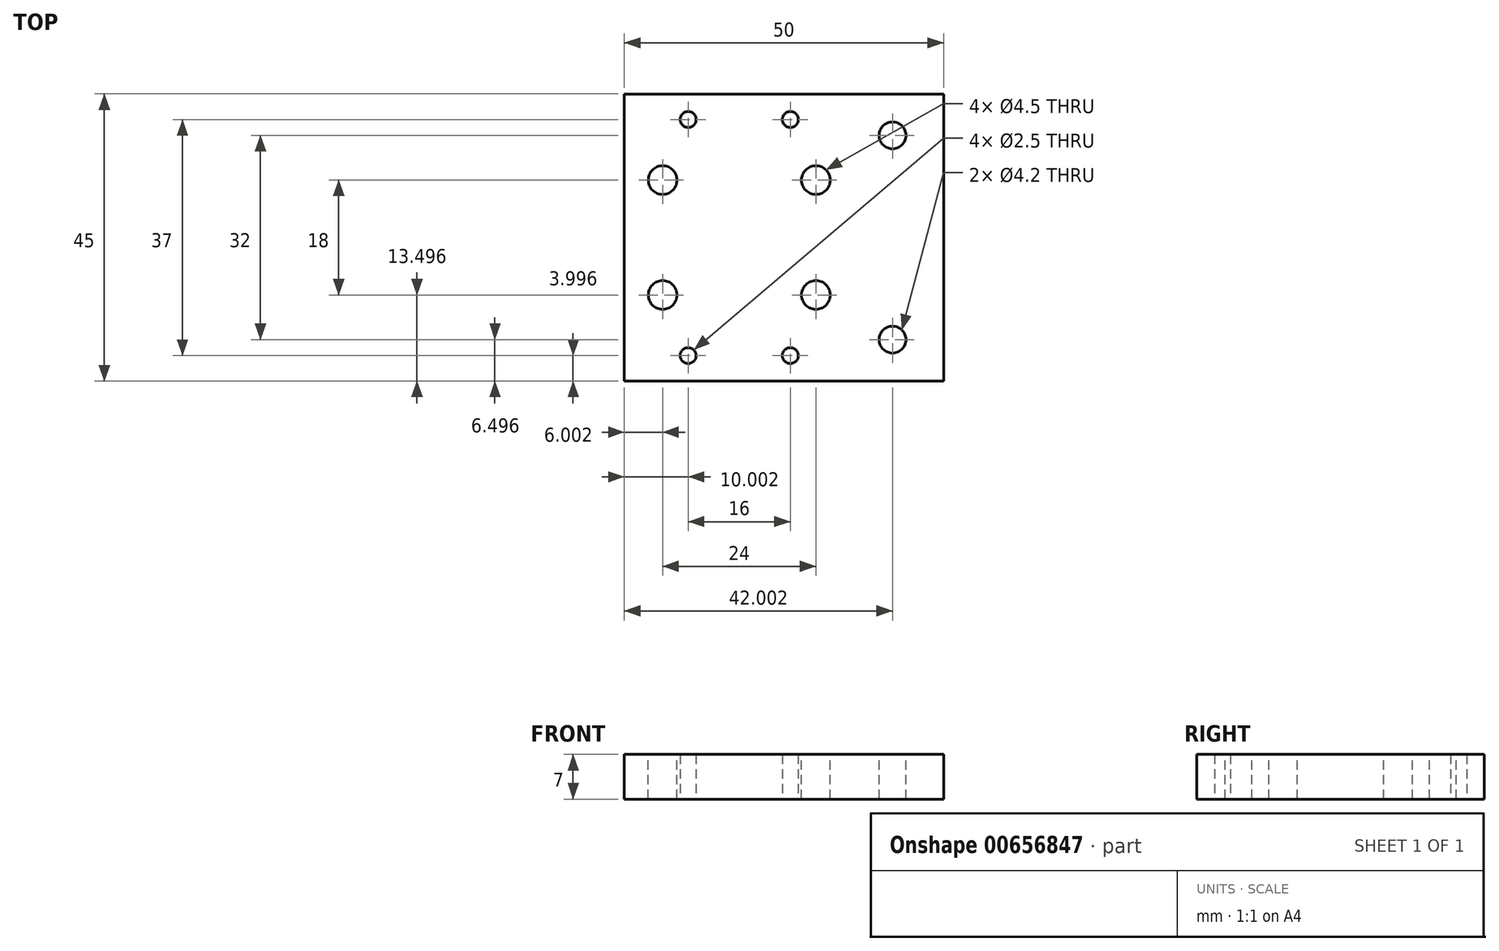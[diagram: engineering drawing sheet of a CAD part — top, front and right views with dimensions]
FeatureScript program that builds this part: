
annotation { "Feature Type Name" : "Feature", "Feature Type Description" : "" }
export const myFeature = defineFeature(function(context is Context, id is Id, definition is map)
    precondition{}
    {
        {
            var Q0;
            Q0=qCreatedBy(makeId("Top.planeOp"),FACE);
            var sketch = newSketch(context, id + "F0", { "sketchPlane" : qUnion([Q0])});
            skLineSegment(sketch, "E0.bottom", {"start": v(-9.8, 26.95) * mm, "end": v(40.2, 26.95) * mm});
            skLineSegment(sketch, "E0.top", {"start": v(-9.8, -18.05) * mm, "end": v(40.2, -18.05) * mm});
            skLineSegment(sketch, "E0.left", {"start": v(-9.8, 26.95) * mm, "end": v(-9.8, -18.05) * mm});
            skLineSegment(sketch, "E0.right", {"start": v(40.2, 26.95) * mm, "end": v(40.2, -18.05) * mm});
            skSolve(sketch);
        }
        {
            var Q0;
            Q0=qSketchRegion(id+"F0",true);
            extrude(context, id + "F1", {"entities" : qUnion([Q0]), "depth" : 7 * mm, "offsetDistance" : 25 * mm});
        }
        {
            var Q0;
            Q0=makeQuery(id+"F1.opExtrude","CAP_FACE",FACE,{"disambiguationData":[OSD([sQuery(id+"F0.wireOp",EDGE,"E0.bottom"),sQuery(id+"F0.wireOp",EDGE,"E0.top"),sQuery(id+"F0.wireOp",EDGE,"E0.left"),sQuery(id+"F0.wireOp",EDGE,"E0.right")])],"isStart":false});
            var sketch = newSketch(context, id + "F2", { "sketchPlane" : qUnion([Q0])});
            skCircle(sketch, "E1", {"center": v(32.2, 20.45) * mm, "radius": 2.1 * mm});
            skLineSegment(sketch, "E2", {"start": v(40.2, 4.45) * mm, "end": v(-9.8, 4.45) * mm});
            skCircle(sketch, "E3.MirrorC", {"center": v(32.2, -11.55) * mm, "radius": 2.1 * mm});
            skSolve(sketch);
        }
        {
            var Q0;
            Q0=sQuery(id+"F2.wireOp",VERTEX,"E1.center");
            var Q1;
            Q1=sQuery(id+"F2.wireOp",VERTEX,"E3.MirrorC.center");
            var Q2;
            Q2=makeQuery(id+"F1.opExtrude","SWEPT_BODY",BODY,{"disambiguationData":[OSD([sQuery(id+"F0.wireOp",EDGE,"E0.bottom"),sQuery(id+"F0.wireOp",EDGE,"E0.top"),sQuery(id+"F0.wireOp",EDGE,"E0.left"),sQuery(id+"F0.wireOp",EDGE,"E0.right")])]});
            hole(context, id + "F3", {"style" : HoleStyle.SIMPLE, "endStyle" : HoleEndStyle.THROUGH, "standardTappedOrClearance" : lookupTablePath({ "standard" : "ISO", "engagement" : "75%", "pitch" : "0.8 mm", "size" : "M5", "type" : "Tapped" }), "standardBlindInLast" : lookupTablePath({ "standard" : "ISO", "engagement" : "75%", "pitch" : "0.8 mm", "size" : "M5", "type" : "Tapped" }), "holeDiameter" : 4.2 * mm, "majorDiameter" : 5 * mm, "showTappedDepth" : true, "isTappedThrough" : true, "tappedDepth" : 12 * mm, "tapClearance" : 3, "locations" : qUnion([Q0, Q1]), "scope" : qUnion([Q2])});
        }
        {
            var Q0;
            Q0=makeQuery(id+"F1.opExtrude","CAP_FACE",FACE,{"disambiguationData":[OSD([sQuery(id+"F0.wireOp",EDGE,"E0.bottom"),sQuery(id+"F0.wireOp",EDGE,"E0.top"),sQuery(id+"F0.wireOp",EDGE,"E0.left"),sQuery(id+"F0.wireOp",EDGE,"E0.right")])],"isStart":false});
            var sketch = newSketch(context, id + "F4", { "sketchPlane" : qUnion([Q0])});
            skCircle(sketch, "E4", {"center": v(-3.8, 13.45) * mm, "radius": 2.25 * mm});
            skLineSegment(sketch, "E5", {"start": v(-9.8, 4.45) * mm, "end": v(40.2, 4.45) * mm});
            skCircle(sketch, "E6.MirrorC", {"center": v(-3.8, -4.55) * mm, "radius": 2.25 * mm});
            skLineSegment(sketch, "E7", {"start": v(8.2, 26.95) * mm, "end": v(8.2, -18.05) * mm});
            skCircle(sketch, "E8.MirrorC", {"center": v(20.2, 13.45) * mm, "radius": 2.25 * mm});
            skCircle(sketch, "E9.MirrorC", {"center": v(20.2, -4.55) * mm, "radius": 2.25 * mm});
            skSolve(sketch);
        }
        {
            var Q0;
            Q0=sQuery(id+"F4.wireOp",VERTEX,"E4.center");
            var Q1;
            Q1=sQuery(id+"F4.wireOp",VERTEX,"E8.MirrorC.center");
            var Q2;
            Q2=sQuery(id+"F4.wireOp",VERTEX,"E9.MirrorC.center");
            var Q3;
            Q3=sQuery(id+"F4.wireOp",VERTEX,"E6.MirrorC.center");
            var Q4;
            Q4=makeQuery(id+"F1.opExtrude","SWEPT_BODY",BODY,{"disambiguationData":[OSD([sQuery(id+"F0.wireOp",EDGE,"E0.bottom"),sQuery(id+"F0.wireOp",EDGE,"E0.top"),sQuery(id+"F0.wireOp",EDGE,"E0.left"),sQuery(id+"F0.wireOp",EDGE,"E0.right")])]});
            hole(context, id + "F5", {"style" : HoleStyle.SIMPLE, "endStyle" : HoleEndStyle.THROUGH, "holeDiameter" : 4.5 * mm, "majorDiameter" : 4 * mm, "isTappedThrough" : true, "tappedDepth" : 12 * mm, "tapClearance" : 3, "locations" : qUnion([Q0, Q1, Q2, Q3]), "scope" : qUnion([Q4])});
        }
        {
            var Q0;
            Q0=makeQuery(id+"F1.opExtrude","CAP_FACE",FACE,{"disambiguationData":[OSD([sQuery(id+"F0.wireOp",EDGE,"E0.bottom"),sQuery(id+"F0.wireOp",EDGE,"E0.top"),sQuery(id+"F0.wireOp",EDGE,"E0.left"),sQuery(id+"F0.wireOp",EDGE,"E0.right")])],"isStart":true});
            var sketch = newSketch(context, id + "F6", { "sketchPlane" : qUnion([Q0])});
            skCircle(sketch, "E10", {"center": v(0.2, 14.05) * mm, "radius": 1.25 * mm});
            skLineSegment(sketch, "E11", {"start": v(8.2, 18.05) * mm, "end": v(8.2, -26.95) * mm});
            skCircle(sketch, "E12.MirrorC", {"center": v(16.2, 14.05) * mm, "radius": 1.25 * mm});
            skLineSegment(sketch, "E13", {"start": v(-3.8, 4.55) * mm, "end": v(-3.8, 18.05) * mm});
            skLineSegment(sketch, "E14", {"start": v(-9.8, -4.45) * mm, "end": v(40.2, -4.45) * mm});
            skCircle(sketch, "E15.MirrorC", {"center": v(0.2, -22.95) * mm, "radius": 1.25 * mm});
            skCircle(sketch, "E16.MirrorC", {"center": v(16.2, -22.95) * mm, "radius": 1.25 * mm});
            skSolve(sketch);
        }
        {
            var Q0;
            Q0=sQuery(id+"F6.wireOp",VERTEX,"E10.center");
            var Q1;
            Q1=sQuery(id+"F6.wireOp",VERTEX,"E12.MirrorC.center");
            var Q2;
            Q2=sQuery(id+"F6.wireOp",VERTEX,"E16.MirrorC.center");
            var Q3;
            Q3=sQuery(id+"F6.wireOp",VERTEX,"E15.MirrorC.center");
            var Q4;
            Q4=makeQuery(id+"F1.opExtrude","SWEPT_BODY",BODY,{"disambiguationData":[OSD([sQuery(id+"F0.wireOp",EDGE,"E0.bottom"),sQuery(id+"F0.wireOp",EDGE,"E0.top"),sQuery(id+"F0.wireOp",EDGE,"E0.left"),sQuery(id+"F0.wireOp",EDGE,"E0.right")])]});
            hole(context, id + "F7", {"style" : HoleStyle.SIMPLE, "endStyle" : HoleEndStyle.THROUGH, "standardTappedOrClearance" : lookupTablePath({ "standard" : "ISO", "engagement" : "75%", "pitch" : "0.5 mm", "size" : "M3", "type" : "Tapped" }), "standardBlindInLast" : lookupTablePath({ "standard" : "ISO", "engagement" : "75%", "pitch" : "0.5 mm", "size" : "M3", "type" : "Tapped" }), "holeDiameter" : 2.5 * mm, "majorDiameter" : 3 * mm, "showTappedDepth" : true, "isTappedThrough" : true, "tappedDepth" : 12 * mm, "tapClearance" : 3, "locations" : qUnion([Q0, Q1, Q2, Q3]), "scope" : qUnion([Q4])});
        }
    });
